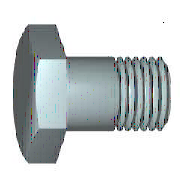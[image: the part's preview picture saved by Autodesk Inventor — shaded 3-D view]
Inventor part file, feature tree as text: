
AUTODESK INVENTOR PART (.ipt)
format: ipt  version: 2022 (Build 260153000, 153)  size: 190,464 bytes
history: native  units: mm (DEFAULTED — no unit token found)
features: sketch x3, extrude x1, chamfer x1, plane x1
ambient origin geometry x7: Origin, YZ Plane, XZ Plane, X Axis, Y Axis, Z Axis, Center Point
bodies: Solid1 (feature_tree), Body (feature_tree)
feature tree (6):
  extrude  "Head"  Depth=22.0mm
  chamfer  "Chamfer1"  Distance=4.7mm
  plane  "Work Plane1"
  sketch  "Sketch1"  dims[d0=70.0mm d1=22.0mm]
  sketch  "Sketch2"  dims[d2=8.0mm]
  sketch  "Sketch4"  dims[d12=90.0deg d3=4.7mm d4=0.0mm d5=30.0deg d21=90.0deg d6=0.766813mm d7=0.766912mm d8=0.0mm d9=0.6001mm d10=11.63mm d11=13.0mm d13=0.766912mm d14=8.0mm d15=22.0mm d16=0.0mm d19=13.0mm d55=45.0deg d57=0.0mm d58=0.0mm]
